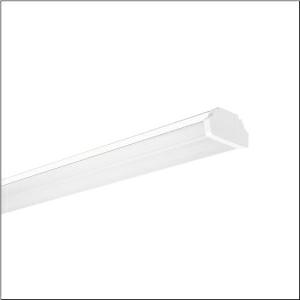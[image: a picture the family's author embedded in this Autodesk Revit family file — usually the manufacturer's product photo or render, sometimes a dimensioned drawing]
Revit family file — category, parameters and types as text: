
# Revit family: dus_r__31_gen_2_53bd812dv4d5d2_d242
name_source: partatom
category: Lighting Fixtures
units: mm (PartAtom-declared; Revit-internal decimal feet)

## family parameters
Cut with Voids When Loaded = No
Host = Face
Light Source = No
Part Type = Normal
Room Calculation Point = No
Round Connector Dimension = Use Diameter
Shared = No

## types (1)
- --- (1 x LED, 13680 lm, 74.9 W, 4000K)
    Apparent Load = 75 VA
    CIE Flux Codes = 47 80 95 93 100
    Color Rendering = 80
    Color Temperature = 4000K
    Default Elevation = 1800 mm
    Description = DUS® 31 Gen.2, luminaire insert, of sheet steel, coil coated, white, length: 1.535mm, width: 81mm, height: 90mm, 5x system unit, system units: 307mm, LED rated luminous flux: 13.680lm, light colour: 840, control gear: DALI 2, control gear: ECG DALI, with plug, 5-pole, with phase selection, mains connection: 220..240V, AC, 50/60Hz, rated input power: 75W, through-wiring accessed according to module size, primary optical cover: cover, of PMMA, light emission: direct distribution, primary light characteristic: symmetric, protection rating (complete): IP20, protection rating (LED compartment): IP50, insulation class (complete): insulation class I (protective earthing), certification: CE, ENEC, VDE, UKCA, impact resistance: IK03, permissible ambient temperature for indoor applications: -25..+35°C, corresponds to IFS (International Featured Standards) requirements for safety and quality in the food industry, reducing of maximum allowable ambient temperature of 5°C with ceiling mounting, packaging unit: 1 piece
    Height = 95 mm
    Lamp = 1 x LED
    Lamp Light Flux = 13680 lm
    Lamp Power = 74.9 W
    Lamp count = 1
    Length = 1535 mm
    Luminous efficacy = 183 lm/W
    Manufacturer = Siteco
    ModVariant = No
    Model = 53BD812DV4D5D2
    Mounting Place = Ceiling
    Mounting Type = Pendant
    Number of Poles = 1
    OnlyDefault = Yes
    Power Factor = 1
    Product Name = DUS® 31 Gen.2
    Product group = luminaire insert
    ProductGroupID = 901
    Protection Class = Protection class I
    Protection Degree = IP 20
    RLX_Detail_Level = 1
    RLX_Emergency_Light_Flux = 0 lm
    RLX_Emergency_Type = 0
    RLX_Emergency_Type_DB = No
    RlxData = <blob elided: 32145 chars, md5=18a14004>
    Socket = socket
    Standby Power = 0 W
    System Light Flux = 13680 lm
    System Power = 75 W
    Type Comments = factory setting: luminous flux: 100 % | dim-lin: 254 | 511 mA
    Type Image = l_1319596.jpg
    URL = http://relux.com
    VarID = @adj_010129
    Voltage = 0 V
    Weight = 0.00 kg
    Width = 81 mm

## geometry (parser evidence)
native form markers: Blend x4, Sweep x14
no freeform markers — native parametric forms only
